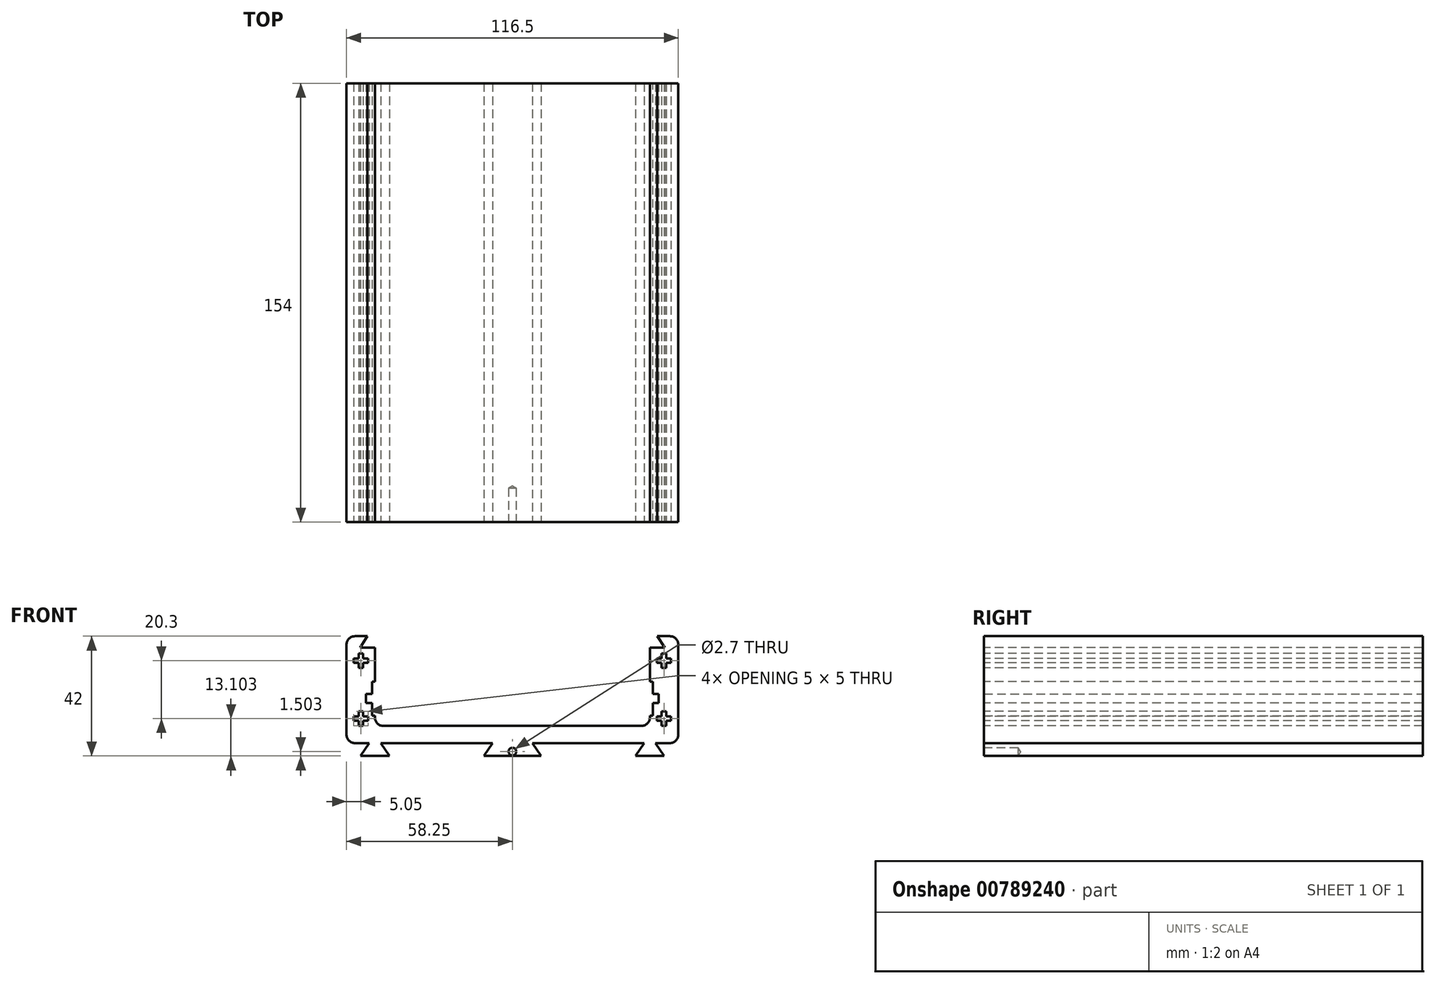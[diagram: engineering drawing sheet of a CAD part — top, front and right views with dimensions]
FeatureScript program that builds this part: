
annotation { "Feature Type Name" : "Feature", "Feature Type Description" : "" }
export const myFeature = defineFeature(function(context is Context, id is Id, definition is map)
    precondition{}
    {
        {
            var Q0;
            Q0=qCreatedBy(makeId("Front.planeOp"),FACE);
            var sketch = newSketch(context, id + "F0", { "sketchPlane" : qUnion([Q0])});
            skLineSegment(sketch, "E0", {"start": v(0, -17) * mm, "end": v(-10.04, -17) * mm});
            skLineSegment(sketch, "E1", {"start": v(-10.04, -17) * mm, "end": v(-7, -12.5) * mm});
            skLineSegment(sketch, "E2", {"start": v(-7, -12.5) * mm, "end": v(-46.25, -12.5) * mm});
            skLineSegment(sketch, "E3", {"start": v(-46.25, -12.5) * mm, "end": v(-43.21, -17) * mm});
            skLineSegment(sketch, "E4", {"start": v(-43.21, -17) * mm, "end": v(-53.29, -17) * mm});
            skLineSegment(sketch, "E5", {"start": v(-53.29, -17) * mm, "end": v(-50.25, -12.5) * mm});
            skLineSegment(sketch, "E6", {"start": v(-50.25, -12.5) * mm, "end": v(-55.25, -12.5) * mm});
            skLineSegment(sketch, "E7", {"start": v(-58.25, -9.5) * mm, "end": v(-58.25, 22) * mm});
            skLineSegment(sketch, "E8", {"start": v(-55.25, 25) * mm, "end": v(-50.87, 25) * mm});
            skLineSegment(sketch, "E9", {"start": v(-50.87, 25) * mm, "end": v(-53.5, 21) * mm});
            skLineSegment(sketch, "E10", {"start": v(-53.5, 21) * mm, "end": v(-48.25, 21) * mm});
            skLineSegment(sketch, "E11", {"start": v(-48.25, 21) * mm, "end": v(-48.25, 4.7) * mm});
            skLineSegment(sketch, "E12", {"start": v(-48.25, 4.7) * mm, "end": v(-51.35, 4.7) * mm});
            skLineSegment(sketch, "E13", {"start": v(-51.35, 4.7) * mm, "end": v(-51.35, 1.5) * mm});
            skLineSegment(sketch, "E14", {"start": v(-51.35, 1.5) * mm, "end": v(-48.25, 1.5) * mm});
            skLineSegment(sketch, "E15", {"start": v(-48.25, 1.5) * mm, "end": v(-48.25, -3.5) * mm});
            skLineSegment(sketch, "E16", {"start": v(-45.25, -6.5) * mm, "end": v(0, -6.5) * mm});
            skLineSegment(sketch, "E17", {"start": v(-48.25, 29.47) * mm, "end": v(-48.25, -26.87) * mm, "construction": true});
            skPoint(sketch, "E18.visualSharp", {"position": v(-58.25, 25) * mm});
            skArc(sketch, "E18.filletArc", {"start": v(-55.25, 25) * mm, "mid": v(-57.37, 24.11) * mm, "end": v(-58.25, 22) * mm});
            skPoint(sketch, "E19.visualSharp", {"position": v(-58.25, -12.5) * mm});
            skArc(sketch, "E19.filletArc", {"start": v(-58.25, -9.5) * mm, "mid": v(-57.37, -11.63) * mm, "end": v(-55.25, -12.5) * mm});
            skPoint(sketch, "E20.visualSharp", {"position": v(-48.25, -6.5) * mm});
            skArc(sketch, "E20.filletArc", {"start": v(-48.25, -3.5) * mm, "mid": v(-47.37, -5.63) * mm, "end": v(-45.25, -6.5) * mm});
            skLineSegment(sketch, "E21", {"start": v(-53.2, 35.2) * mm, "end": v(-53.2, -9.28) * mm, "construction": true});
            skLineSegment(sketch, "E22", {"start": v(-92.18, 6.24) * mm, "end": v(0, 6.24) * mm, "construction": true});
            skArc(sketch, "E23.MirrorCS", {"start": v(48.25, -3.5) * mm, "mid": v(47.37, -5.63) * mm, "end": v(45.25, -6.5) * mm});
            skArc(sketch, "E24.MirrorCS", {"start": v(55.25, 25) * mm, "mid": v(57.37, 24.11) * mm, "end": v(58.25, 22) * mm});
            skLineSegment(sketch, "E25.MirrorCS", {"start": v(48.25, 1.5) * mm, "end": v(48.25, -3.5) * mm});
            skLineSegment(sketch, "E26.MirrorCS", {"start": v(46.25, -12.5) * mm, "end": v(43.21, -17) * mm});
            skLineSegment(sketch, "E27.MirrorCS", {"start": v(51.35, 4.7) * mm, "end": v(51.35, 1.5) * mm});
            skLineSegment(sketch, "E28.MirrorCS", {"start": v(53.29, -17) * mm, "end": v(50.25, -12.5) * mm});
            skLineSegment(sketch, "E29.MirrorCS", {"start": v(10.04, -17) * mm, "end": v(7, -12.5) * mm});
            skLineSegment(sketch, "E30.MirrorCS", {"start": v(48.25, 4.7) * mm, "end": v(51.35, 4.7) * mm});
            skLineSegment(sketch, "E31.MirrorCS", {"start": v(51.35, 1.5) * mm, "end": v(48.25, 1.5) * mm});
            skArc(sketch, "E32.MirrorCS", {"start": v(58.25, -9.5) * mm, "mid": v(57.37, -11.63) * mm, "end": v(55.25, -12.5) * mm});
            skLineSegment(sketch, "E33.MirrorCS", {"start": v(45.25, -6.5) * mm, "end": v(0, -6.5) * mm});
            skLineSegment(sketch, "E34.MirrorCS", {"start": v(48.25, 29.47) * mm, "end": v(48.25, -26.87) * mm, "construction": true});
            skLineSegment(sketch, "E35.MirrorCS", {"start": v(0, -17) * mm, "end": v(10.04, -17) * mm});
            skPoint(sketch, "E36.MirrorP", {"position": v(58.25, -12.5) * mm});
            skLineSegment(sketch, "E37.MirrorCS", {"start": v(7, -12.5) * mm, "end": v(46.25, -12.5) * mm});
            skLineSegment(sketch, "E38.MirrorCS", {"start": v(43.21, -17) * mm, "end": v(53.29, -17) * mm});
            skPoint(sketch, "E39.MirrorP", {"position": v(58.25, 25) * mm});
            skLineSegment(sketch, "E40.MirrorCS", {"start": v(50.25, -12.5) * mm, "end": v(55.25, -12.5) * mm});
            skLineSegment(sketch, "E41.MirrorCS", {"start": v(53.2, 35.2) * mm, "end": v(53.2, -9.28) * mm, "construction": true});
            skPoint(sketch, "E42.MirrorP", {"position": v(48.25, -6.5) * mm});
            skLineSegment(sketch, "E43.MirrorCS", {"start": v(58.25, -9.5) * mm, "end": v(58.25, 22) * mm});
            skLineSegment(sketch, "E44.MirrorCS", {"start": v(53.5, 21) * mm, "end": v(48.25, 21) * mm});
            skLineSegment(sketch, "E45.MirrorCS", {"start": v(48.25, 21) * mm, "end": v(48.25, 4.7) * mm});
            skLineSegment(sketch, "E46.MirrorCS", {"start": v(55.25, 25) * mm, "end": v(50.87, 25) * mm});
            skLineSegment(sketch, "E47.MirrorCS", {"start": v(50.87, 25) * mm, "end": v(53.5, 21) * mm});
            skPoint(sketch, "E48", {"position": v(-53.2, 16.4) * mm});
            skPoint(sketch, "E49", {"position": v(-53.2, -3.9) * mm});
            skLineSegment(sketch, "E50", {"start": v(-55.7, 17.2) * mm, "end": v(-54, 17.2) * mm});
            skLineSegment(sketch, "E51", {"start": v(-54, 17.2) * mm, "end": v(-54, 18.9) * mm});
            skLineSegment(sketch, "E52", {"start": v(-54, 18.9) * mm, "end": v(-52.4, 18.9) * mm});
            skLineSegment(sketch, "E53", {"start": v(-52.4, 18.9) * mm, "end": v(-52.4, 17.2) * mm});
            skLineSegment(sketch, "E54", {"start": v(-52.4, 17.2) * mm, "end": v(-50.7, 17.2) * mm});
            skLineSegment(sketch, "E55", {"start": v(-50.7, 17.2) * mm, "end": v(-50.7, 15.6) * mm});
            skLineSegment(sketch, "E56", {"start": v(-50.7, 15.6) * mm, "end": v(-52.4, 15.6) * mm});
            skLineSegment(sketch, "E57", {"start": v(-52.4, 15.6) * mm, "end": v(-52.4, 13.9) * mm});
            skLineSegment(sketch, "E58", {"start": v(-52.4, 13.9) * mm, "end": v(-54, 13.9) * mm});
            skLineSegment(sketch, "E59", {"start": v(-54, 13.9) * mm, "end": v(-54, 15.6) * mm});
            skLineSegment(sketch, "E60", {"start": v(-54, 15.6) * mm, "end": v(-55.7, 15.6) * mm});
            skLineSegment(sketch, "E61", {"start": v(-55.7, 15.6) * mm, "end": v(-55.7, 17.2) * mm});
            skLineSegment(sketch, "E62", {"start": v(-50.4, 16.4) * mm, "end": v(-59.4, 16.4) * mm, "construction": true});
            skLineSegment(sketch, "E63", {"start": v(-49.34, -3.9) * mm, "end": v(-57.36, -3.9) * mm, "construction": true});
            skLineSegment(sketch, "E64", {"start": v(-54, -1.4) * mm, "end": v(-52.4, -1.4) * mm});
            skLineSegment(sketch, "E65", {"start": v(-52.4, -1.4) * mm, "end": v(-52.4, -3.1) * mm});
            skLineSegment(sketch, "E66", {"start": v(-52.4, -3.1) * mm, "end": v(-50.7, -3.1) * mm});
            skLineSegment(sketch, "E67", {"start": v(-50.7, -3.1) * mm, "end": v(-50.7, -4.7) * mm});
            skLineSegment(sketch, "E68", {"start": v(-50.7, -4.7) * mm, "end": v(-52.4, -4.7) * mm});
            skLineSegment(sketch, "E69", {"start": v(-52.4, -4.7) * mm, "end": v(-52.4, -6.4) * mm});
            skLineSegment(sketch, "E70", {"start": v(-52.4, -6.4) * mm, "end": v(-54, -6.4) * mm});
            skLineSegment(sketch, "E71", {"start": v(-54, -6.4) * mm, "end": v(-54, -4.7) * mm});
            skLineSegment(sketch, "E72", {"start": v(-54, -4.7) * mm, "end": v(-55.7, -4.7) * mm});
            skLineSegment(sketch, "E73", {"start": v(-55.7, -4.7) * mm, "end": v(-55.7, -3.1) * mm});
            skLineSegment(sketch, "E74", {"start": v(-55.7, -3.1) * mm, "end": v(-54, -3.1) * mm});
            skLineSegment(sketch, "E75", {"start": v(-54, -3.1) * mm, "end": v(-54, -1.4) * mm});
            skLineSegment(sketch, "E76.MirrorCS", {"start": v(54, 17.2) * mm, "end": v(54, 18.9) * mm});
            skLineSegment(sketch, "E77.MirrorCS", {"start": v(54, 18.9) * mm, "end": v(52.4, 18.9) * mm});
            skLineSegment(sketch, "E78.MirrorCS", {"start": v(52.4, 18.9) * mm, "end": v(52.4, 17.2) * mm});
            skLineSegment(sketch, "E79.MirrorCS", {"start": v(52.4, 17.2) * mm, "end": v(50.7, 17.2) * mm});
            skLineSegment(sketch, "E80.MirrorCS", {"start": v(50.7, 17.2) * mm, "end": v(50.7, 15.6) * mm});
            skLineSegment(sketch, "E81.MirrorCS", {"start": v(50.7, 15.6) * mm, "end": v(52.4, 15.6) * mm});
            skLineSegment(sketch, "E82.MirrorCS", {"start": v(52.4, 15.6) * mm, "end": v(52.4, 13.9) * mm});
            skLineSegment(sketch, "E83.MirrorCS", {"start": v(52.4, 13.9) * mm, "end": v(54, 13.9) * mm});
            skLineSegment(sketch, "E84.MirrorCS", {"start": v(54, 13.9) * mm, "end": v(54, 15.6) * mm});
            skLineSegment(sketch, "E85.MirrorCS", {"start": v(54, 15.6) * mm, "end": v(55.7, 15.6) * mm});
            skLineSegment(sketch, "E86.MirrorCS", {"start": v(55.7, 15.6) * mm, "end": v(55.7, 17.2) * mm});
            skLineSegment(sketch, "E87.MirrorCS", {"start": v(55.7, 17.2) * mm, "end": v(54, 17.2) * mm});
            skLineSegment(sketch, "E88.MirrorCS", {"start": v(54, -1.4) * mm, "end": v(52.4, -1.4) * mm});
            skLineSegment(sketch, "E89.MirrorCS", {"start": v(52.4, -1.4) * mm, "end": v(52.4, -3.1) * mm});
            skLineSegment(sketch, "E90.MirrorCS", {"start": v(52.4, -3.1) * mm, "end": v(50.7, -3.1) * mm});
            skLineSegment(sketch, "E91.MirrorCS", {"start": v(50.7, -3.1) * mm, "end": v(50.7, -4.7) * mm});
            skLineSegment(sketch, "E92.MirrorCS", {"start": v(50.7, -4.7) * mm, "end": v(52.4, -4.7) * mm});
            skLineSegment(sketch, "E93.MirrorCS", {"start": v(52.4, -4.7) * mm, "end": v(52.4, -6.4) * mm});
            skLineSegment(sketch, "E94.MirrorCS", {"start": v(52.4, -6.4) * mm, "end": v(54, -6.4) * mm});
            skLineSegment(sketch, "E95.MirrorCS", {"start": v(54, -6.4) * mm, "end": v(54, -4.7) * mm});
            skLineSegment(sketch, "E96.MirrorCS", {"start": v(54, -4.7) * mm, "end": v(55.7, -4.7) * mm});
            skLineSegment(sketch, "E97.MirrorCS", {"start": v(55.7, -4.7) * mm, "end": v(55.7, -3.1) * mm});
            skLineSegment(sketch, "E98.MirrorCS", {"start": v(55.7, -3.1) * mm, "end": v(54, -3.1) * mm});
            skLineSegment(sketch, "E99.MirrorCS", {"start": v(54, -3.1) * mm, "end": v(54, -1.4) * mm});
            skSolve(sketch);
        }
        {
            var Q0;
            Q0=qSketchRegion(id+"F0",true);
            extrude(context, id + "F1", {"entities" : qUnion([Q0]), "oppositeDirection" : true, "depth" : 154 * mm, "offsetDistance" : 25 * mm});
        }
        {
            var Q0;
            Q0=makeQuery(id+"F1.opExtrude","CAP_FACE",FACE,{"disambiguationData":[OSD([sQuery(id+"F0.wireOp",EDGE,"E0"),sQuery(id+"F0.wireOp",EDGE,"E1"),sQuery(id+"F0.wireOp",EDGE,"E2"),sQuery(id+"F0.wireOp",EDGE,"E3"),sQuery(id+"F0.wireOp",EDGE,"E4"),sQuery(id+"F0.wireOp",EDGE,"E5"),sQuery(id+"F0.wireOp",EDGE,"E6"),sQuery(id+"F0.wireOp",EDGE,"E7"),sQuery(id+"F0.wireOp",EDGE,"E8"),sQuery(id+"F0.wireOp",EDGE,"E9"),sQuery(id+"F0.wireOp",EDGE,"E10"),sQuery(id+"F0.wireOp",EDGE,"E11"),sQuery(id+"F0.wireOp",EDGE,"E12"),sQuery(id+"F0.wireOp",EDGE,"E13"),sQuery(id+"F0.wireOp",EDGE,"E14"),sQuery(id+"F0.wireOp",EDGE,"E15"),sQuery(id+"F0.wireOp",EDGE,"E16"),sQuery(id+"F0.wireOp",EDGE,"E18.filletArc"),sQuery(id+"F0.wireOp",EDGE,"E19.filletArc"),sQuery(id+"F0.wireOp",EDGE,"E20.filletArc"),sQuery(id+"F0.wireOp",EDGE,"5194898a-ef6c-4157-a49c-2c8236cce61c"),sQuery(id+"F0.wireOp",EDGE,"7f281998-eedb-455a-a055-9dc59b9fbc9e"),sQuery(id+"F0.wireOp",EDGE,"E23.MirrorCS"),sQuery(id+"F0.wireOp",EDGE,"E24.MirrorCS"),sQuery(id+"F0.wireOp",EDGE,"E25.MirrorCS"),sQuery(id+"F0.wireOp",EDGE,"E26.MirrorCS"),sQuery(id+"F0.wireOp",EDGE,"E27.MirrorCS"),sQuery(id+"F0.wireOp",EDGE,"E28.MirrorCS"),sQuery(id+"F0.wireOp",EDGE,"E29.MirrorCS"),sQuery(id+"F0.wireOp",EDGE,"E30.MirrorCS"),sQuery(id+"F0.wireOp",EDGE,"E31.MirrorCS"),sQuery(id+"F0.wireOp",EDGE,"d584a0aa-b8c3-4ab9-8824-3ea712040d109.MirrorC"),sQuery(id+"F0.wireOp",EDGE,"E32.MirrorCS"),sQuery(id+"F0.wireOp",EDGE,"E241.MirrorC"),sQuery(id+"F0.wireOp",EDGE,"E33.MirrorCS"),sQuery(id+"F0.wireOp",EDGE,"E35.MirrorCS"),sQuery(id+"F0.wireOp",EDGE,"E37.MirrorCS"),sQuery(id+"F0.wireOp",EDGE,"E38.MirrorCS"),sQuery(id+"F0.wireOp",EDGE,"E40.MirrorCS"),sQuery(id+"F0.wireOp",EDGE,"E43.MirrorCS"),sQuery(id+"F0.wireOp",EDGE,"E44.MirrorCS"),sQuery(id+"F0.wireOp",EDGE,"E45.MirrorCS"),sQuery(id+"F0.wireOp",EDGE,"E46.MirrorCS"),sQuery(id+"F0.wireOp",EDGE,"E47.MirrorCS")])],"isStart":true});
            var sketch = newSketch(context, id + "F2", { "sketchPlane" : qUnion([Q0])});
            skPoint(sketch, "E100", {"position": v(0, -15.5) * mm});
            skSolve(sketch);
        }
        {
            var Q0;
            Q0=sQuery(id+"F2.wireOp",VERTEX,"E100");
            var Q1;
            Q1=makeQuery(id+"F1.opExtrude","SWEPT_BODY",BODY,{"disambiguationData":[OSD([sQuery(id+"F0.wireOp",EDGE,"E0"),sQuery(id+"F0.wireOp",EDGE,"E1"),sQuery(id+"F0.wireOp",EDGE,"E2"),sQuery(id+"F0.wireOp",EDGE,"E3"),sQuery(id+"F0.wireOp",EDGE,"E4"),sQuery(id+"F0.wireOp",EDGE,"E5"),sQuery(id+"F0.wireOp",EDGE,"E6"),sQuery(id+"F0.wireOp",EDGE,"E7"),sQuery(id+"F0.wireOp",EDGE,"E8"),sQuery(id+"F0.wireOp",EDGE,"E9"),sQuery(id+"F0.wireOp",EDGE,"E10"),sQuery(id+"F0.wireOp",EDGE,"E11"),sQuery(id+"F0.wireOp",EDGE,"E12"),sQuery(id+"F0.wireOp",EDGE,"E13"),sQuery(id+"F0.wireOp",EDGE,"E14"),sQuery(id+"F0.wireOp",EDGE,"E15"),sQuery(id+"F0.wireOp",EDGE,"E16"),sQuery(id+"F0.wireOp",EDGE,"E18.filletArc"),sQuery(id+"F0.wireOp",EDGE,"E19.filletArc"),sQuery(id+"F0.wireOp",EDGE,"E20.filletArc"),sQuery(id+"F0.wireOp",EDGE,"5194898a-ef6c-4157-a49c-2c8236cce61c"),sQuery(id+"F0.wireOp",EDGE,"7f281998-eedb-455a-a055-9dc59b9fbc9e"),sQuery(id+"F0.wireOp",EDGE,"E23.MirrorCS"),sQuery(id+"F0.wireOp",EDGE,"E24.MirrorCS"),sQuery(id+"F0.wireOp",EDGE,"E25.MirrorCS"),sQuery(id+"F0.wireOp",EDGE,"E26.MirrorCS"),sQuery(id+"F0.wireOp",EDGE,"E27.MirrorCS"),sQuery(id+"F0.wireOp",EDGE,"E28.MirrorCS"),sQuery(id+"F0.wireOp",EDGE,"E29.MirrorCS"),sQuery(id+"F0.wireOp",EDGE,"E30.MirrorCS"),sQuery(id+"F0.wireOp",EDGE,"E31.MirrorCS"),sQuery(id+"F0.wireOp",EDGE,"d584a0aa-b8c3-4ab9-8824-3ea712040d109.MirrorC"),sQuery(id+"F0.wireOp",EDGE,"E32.MirrorCS"),sQuery(id+"F0.wireOp",EDGE,"E241.MirrorC"),sQuery(id+"F0.wireOp",EDGE,"E33.MirrorCS"),sQuery(id+"F0.wireOp",EDGE,"E35.MirrorCS"),sQuery(id+"F0.wireOp",EDGE,"E37.MirrorCS"),sQuery(id+"F0.wireOp",EDGE,"E38.MirrorCS"),sQuery(id+"F0.wireOp",EDGE,"E40.MirrorCS"),sQuery(id+"F0.wireOp",EDGE,"E43.MirrorCS"),sQuery(id+"F0.wireOp",EDGE,"E44.MirrorCS"),sQuery(id+"F0.wireOp",EDGE,"E45.MirrorCS"),sQuery(id+"F0.wireOp",EDGE,"E46.MirrorCS"),sQuery(id+"F0.wireOp",EDGE,"E47.MirrorCS")])]});
            hole(context, id + "F3", {"style" : HoleStyle.SIMPLE, "holeDiameter" : 2.7 * mm, "endStyle" : HoleEndStyle.BLIND, "holeDepth" : 12 * mm, "locations" : qUnion([Q0]), "scope" : qUnion([Q1])});
        }
        {
            var Q0;
            Q0=makeQuery(id+"F1.opExtrude","SWEPT_FACE",FACE,{"disambiguationData":[OSD([sQuery(id+"F0.wireOp",EDGE,"E11")])]});
            var sketch = newSketch(context, id + "F4", { "sketchPlane" : qUnion([Q0])});
            skLineSegment(sketch, "E101.bottom", {"start": v(0, 9.1) * mm, "end": v(154, 9.1) * mm});
            skLineSegment(sketch, "E101.top", {"start": v(0, -2.9) * mm, "end": v(154, -2.9) * mm});
            skLineSegment(sketch, "E101.left", {"start": v(0, 9.1) * mm, "end": v(0, -2.9) * mm});
            skLineSegment(sketch, "E101.right", {"start": v(154, 9.1) * mm, "end": v(154, -2.9) * mm});
            skSolve(sketch);
        }
        {
            var Q0;
            Q0 = qSketchRegion(id + "F4", true);
            extrude(context, id + "F5", {"entities" : qUnion([Q0]), "operationType" : NewBodyOperationType.REMOVE, "oppositeDirection" : true, "depth" : 1 * mm, "offsetDistance" : 25 * mm});
        }
        {
            var Q0;
            Q0=makeQuery(id+"F1.opExtrude","SWEPT_FACE",FACE,{"disambiguationData":[OSD([sQuery(id+"F0.wireOp",EDGE,"E45.MirrorCS")])]});
            var sketch = newSketch(context, id + "F6", { "sketchPlane" : qUnion([Q0])});
            skLineSegment(sketch, "E102.bottom", {"start": v(-154, 9.1) * mm, "end": v(0, 9.1) * mm});
            skLineSegment(sketch, "E102.top", {"start": v(-154, -2.9) * mm, "end": v(0, -2.9) * mm});
            skLineSegment(sketch, "E102.left", {"start": v(-154, 9.1) * mm, "end": v(-154, -2.9) * mm});
            skLineSegment(sketch, "E102.right", {"start": v(0, 9.1) * mm, "end": v(0, -2.9) * mm});
            skSolve(sketch);
        }
        {
            var Q0;
            Q0 = qSketchRegion(id + "F6", true);
            extrude(context, id + "F7", {"entities" : qUnion([Q0]), "operationType" : NewBodyOperationType.REMOVE, "oppositeDirection" : true, "depth" : 1 * mm, "offsetDistance" : 25 * mm});
        }
    });
